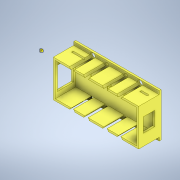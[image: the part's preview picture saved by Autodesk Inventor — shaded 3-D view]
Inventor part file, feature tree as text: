
AUTODESK INVENTOR PART (.ipt)
format: ipt  version: 2021.2 (Build 252289000, 289)  size: 549,888 bytes
history: native  units: in
note: dims shown in document units (in); Inventor stores cm internally (conversion verified against a paired STEP export)
features: sketch x13, extrude x11, hole x2, mirror x2
ambient origin geometry x8: Origin, YZ Plane, XZ Plane, XY Plane, X Axis, Y Axis, Z Axis, Center Point
bodies: Solid1 (feature_tree)
feature tree (28):
  extrude  "Extrusion1"  Depth=4.5in
  extrude  "Extrusion2"  TaperAngle=0.0deg  [1 undecoded]
  hole  "Hole1"  [1 undecoded]
  extrude  "Extrusion3"  Depth=0.875in
  extrude  "Extrusion4"  TaperAngle=0.0deg  [1 undecoded]
  extrude  "Extrusion5"  Depth=2.0in
  extrude  "Extrusion6"  Depth=0.25in
  extrude  "Extrusion7"  Depth=0.1in
  mirror  "Mirror1"
  extrude  "Extrusion8"  Depth=0.6in
  mirror  "Mirror2"
  hole  "Hole2"  [1 undecoded]
  extrude  "Extrusion9"  Depth=1.2in
  extrude  "Extrusion10"  Depth=0.1in
  extrude  "Extrusion11"  TaperAngle=90.0deg  [1 undecoded]
  sketch  "Sketch1"  dims[d0=2.3in d1=4.5in]
  sketch  "Sketch2"  dims[d2=0.1in d3=0.0in]
  sketch  "Sketch3"  dims[d4=0.1in d5=0.1in]
  sketch  "Sketch4"  dims[d6=0.875in d7=0.875in]
  sketch  "Sketch5"  dims[d8=1.08in d9=0.0in]
  sketch  "Sketch6"  dims[d10=1.0in d11=2.0in]
  sketch  "Sketch7"  dims[d12=0.15in d13=0.75in d14=0.279in d15=0.25in d16=0.5635in d17=1.0in d18=0.8108in d19=0.3in]
  sketch  "Sketch8"  dims[d20=0.0in d21=0.0in d22=0.1in]
  sketch  "Sketch9"  dims[d23=0.0in d24=0.6in]
  sketch  "Sketch10"  dims[d25=0.75in d26=0.1in]
  sketch  "Sketch11"  dims[d27=0.0in d28=1.2in]
  sketch  "Sketch12"  dims[d29=0.85in d30=0.1in]
  sketch  "Sketch13"  dims[d31=0.0in d32=90.0deg d33=135.0deg d34=0.05in d35=0.75in d36=0.65in d37=0.0in d38=1.1in d39=0.0in d40=2.5in d41=2.0in d42=0.275in d43=0.75in d44=0.507in d45=0.25in d46=0.5635in d47=1.0in d48=0.8108in d49=0.05in d50=0.0in d51=0.25in d52=0.0in d53=0.25in d54=0.0in]
note: 5 required parameter values undecoded (feature->parameter linkage not recoverable at this tier; creation-order binding heuristic only, values carry confidence <= 0.55)
